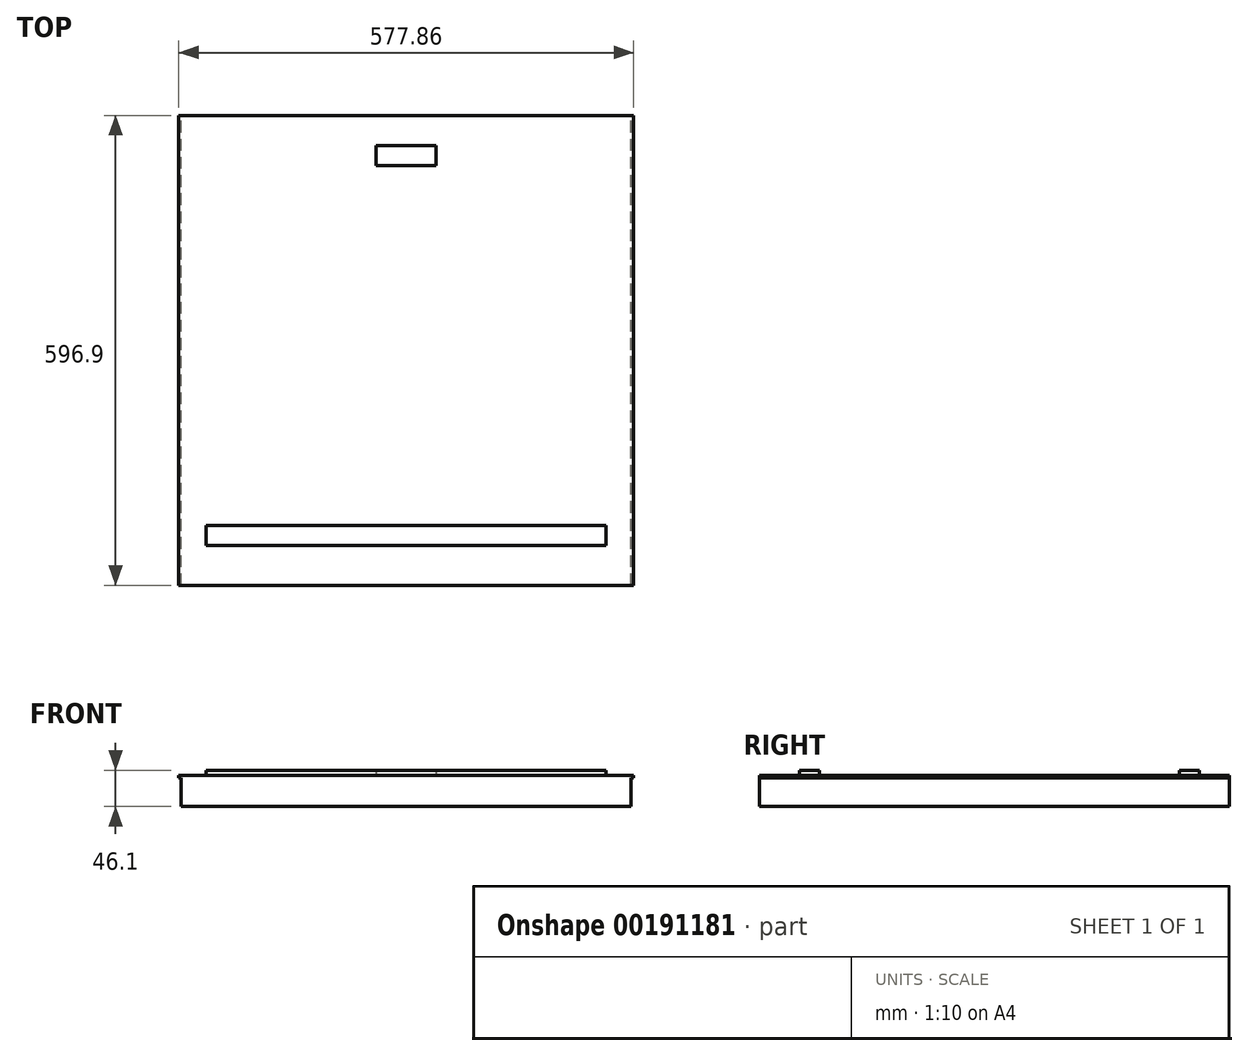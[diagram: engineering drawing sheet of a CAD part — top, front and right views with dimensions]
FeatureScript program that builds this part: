
annotation { "Feature Type Name" : "Feature", "Feature Type Description" : "" }
export const myFeature = defineFeature(function(context is Context, id is Id, definition is map)
    precondition{}
    {
        {
            var Q0;
            Q0=qCreatedBy(makeId("Top.planeOp"),FACE);
            var sketch = newSketch(context, id + "F0", { "sketchPlane" : qUnion([Q0])});
            skLineSegment(sketch, "E0.bottom", {"start": v(285.75, -298.45) * mm, "end": v(-285.75, -298.45) * mm});
            skLineSegment(sketch, "E0.top", {"start": v(285.75, 298.45) * mm, "end": v(-285.75, 298.45) * mm});
            skLineSegment(sketch, "E0.left", {"start": v(285.75, -298.45) * mm, "end": v(285.75, 298.45) * mm});
            skLineSegment(sketch, "E0.right", {"start": v(-285.75, -298.45) * mm, "end": v(-285.75, 298.45) * mm});
            skPoint(sketch, "E0.middle", {"position": v(0, 0) * mm});
            skSolve(sketch);
        }
        {
            var Q0;
            Q0=qSketchRegion(id+"F0",true);
            extrude(context, id + "F1", {"entities" : qUnion([Q0]), "depth" : 36.58 * mm});
        }
        {
            var Q0;
            Q0=makeQuery(id+"F1.opExtrude","CAP_FACE",FACE,{"disambiguationData":[OSD([sQuery(id+"F0.wireOp",EDGE,"E0.bottom"),sQuery(id+"F0.wireOp",EDGE,"E0.top"),sQuery(id+"F0.wireOp",EDGE,"E0.left"),sQuery(id+"F0.wireOp",EDGE,"E0.right")])],"isStart":false});
            var sketch = newSketch(context, id + "F2", { "sketchPlane" : qUnion([Q0])});
            skLineSegment(sketch, "E1.bottom", {"start": v(288.93, -298.45) * mm, "end": v(-288.92, -298.45) * mm});
            skLineSegment(sketch, "E1.top", {"start": v(288.92, 298.45) * mm, "end": v(-288.93, 298.45) * mm});
            skLineSegment(sketch, "E1.left", {"start": v(288.93, -298.45) * mm, "end": v(288.92, 298.45) * mm});
            skLineSegment(sketch, "E1.right", {"start": v(-288.92, -298.45) * mm, "end": v(-288.93, 298.45) * mm});
            skPoint(sketch, "E1.middle", {"position": v(0, 0) * mm});
            skSolve(sketch);
        }
        {
            var Q0;
            Q0 = qSketchRegion(id + "F2", true);
            extrude(context, id + "F3", {"entities" : qUnion([Q0]), "operationType" : NewBodyOperationType.ADD, "depth" : 3.17 * mm});
        }
        {
            var Q0;
            Q0=makeQuery(id+"F3.opExtrude","CAP_FACE",FACE,{"disambiguationData":[OSD([sQuery(id+"F2.wireOp",EDGE,"E1.bottom"),sQuery(id+"F2.wireOp",EDGE,"E1.top"),sQuery(id+"F2.wireOp",EDGE,"E1.left"),sQuery(id+"F2.wireOp",EDGE,"E1.right")])],"isStart":false});
            var sketch = newSketch(context, id + "F4", { "sketchPlane" : qUnion([Q0])});
            skLineSegment(sketch, "E2.bottom", {"start": v(-254, -222.25) * mm, "end": v(254, -222.25) * mm});
            skLineSegment(sketch, "E2.top", {"start": v(-254, -247.65) * mm, "end": v(254, -247.65) * mm});
            skLineSegment(sketch, "E2.left", {"start": v(-254, -222.25) * mm, "end": v(-254, -247.65) * mm});
            skLineSegment(sketch, "E2.right", {"start": v(254, -222.25) * mm, "end": v(254, -247.65) * mm});
            skPoint(sketch, "E3", {"position": v(0, -234.95) * mm});
            skLineSegment(sketch, "E4", {"start": v(0, 83.52) * mm, "end": v(0, -89.55) * mm, "construction": true});
            skLineSegment(sketch, "E5.bottom", {"start": v(38.1, 234.95) * mm, "end": v(-38.1, 234.95) * mm});
            skLineSegment(sketch, "E5.top", {"start": v(38.1, 260.35) * mm, "end": v(-38.1, 260.35) * mm});
            skLineSegment(sketch, "E5.left", {"start": v(38.1, 234.95) * mm, "end": v(38.1, 260.35) * mm});
            skLineSegment(sketch, "E5.right", {"start": v(-38.1, 234.95) * mm, "end": v(-38.1, 260.35) * mm});
            skPoint(sketch, "E5.middle", {"position": v(0, 247.65) * mm});
            skSolve(sketch);
        }
        {
            var Q0;
            Q0 = qSketchRegion(id + "F4", true);
            extrude(context, id + "F5", {"entities" : qUnion([Q0]), "operationType" : NewBodyOperationType.ADD, "depth" : 6.35 * mm});
        }
    });
